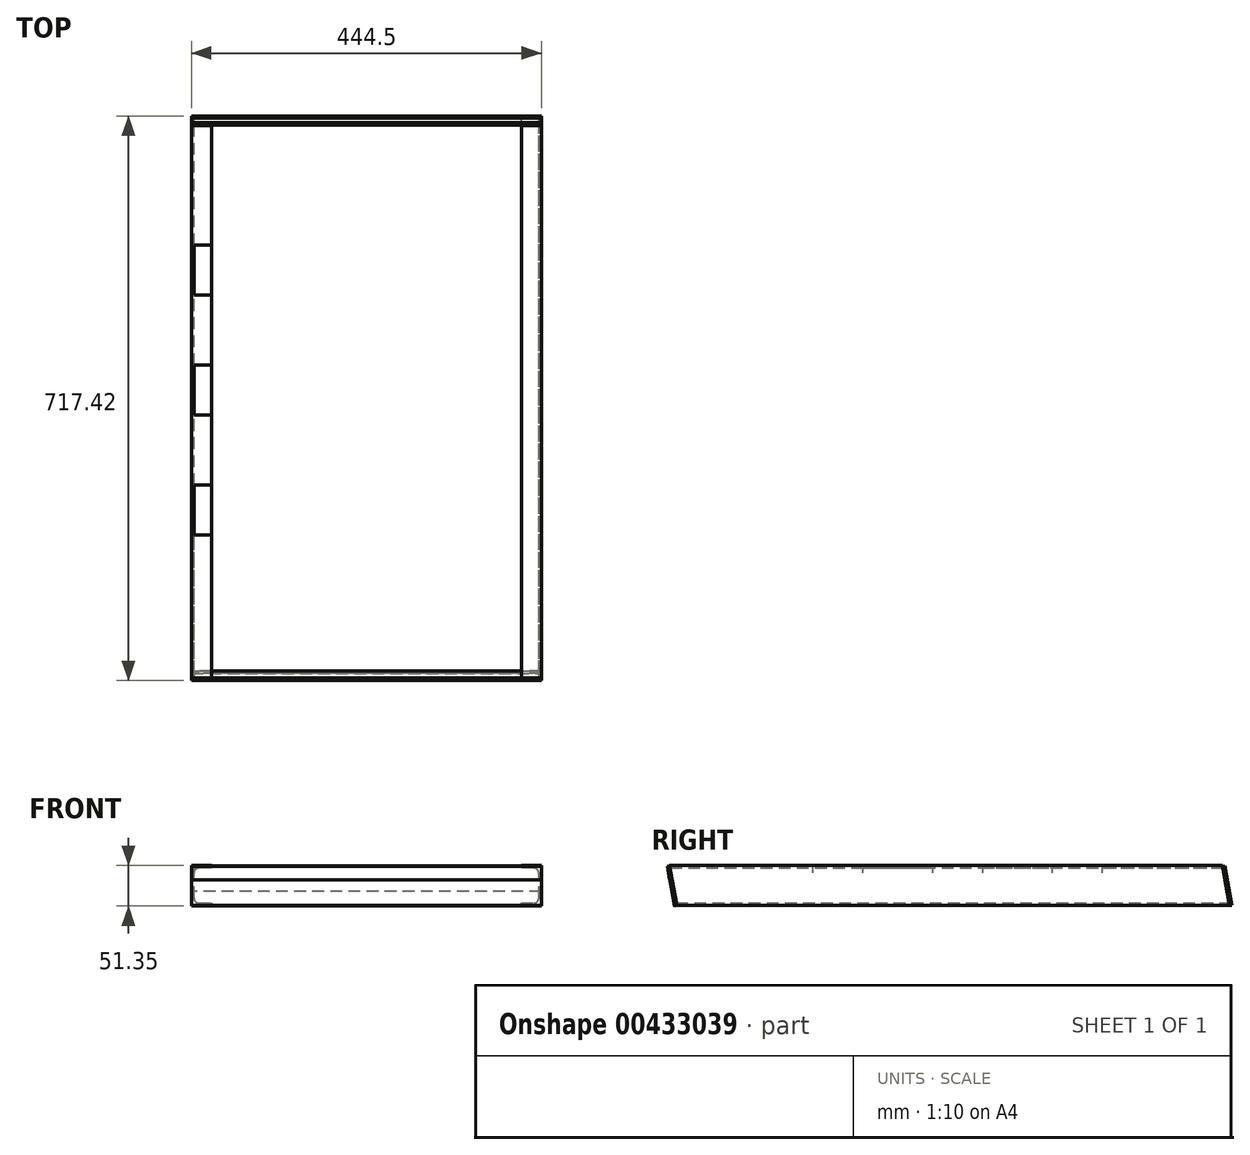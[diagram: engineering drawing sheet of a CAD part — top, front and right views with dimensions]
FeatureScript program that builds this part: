
annotation { "Feature Type Name" : "Feature", "Feature Type Description" : "" }
export const myFeature = defineFeature(function(context is Context, id is Id, definition is map)
    precondition{}
    {
        {
            var Q0;
            Q0=qCreatedBy(makeId("Front.planeOp"),FACE);
            var sketch = newSketch(context, id + "F0", { "sketchPlane" : qUnion([Q0])});
            skLineSegment(sketch, "E0", {"start": v(25.4, 50.8) * mm, "end": v(0, 50.8) * mm});
            skLineSegment(sketch, "E1", {"start": v(0, 50.8) * mm, "end": v(0, 0) * mm});
            skLineSegment(sketch, "E2", {"start": v(0, 0) * mm, "end": v(25.4, 0) * mm});
            skLineSegment(sketch, "E3", {"start": v(25.4, 0) * mm, "end": v(25.4, 3.18) * mm});
            skLineSegment(sketch, "E4", {"start": v(25.4, 3.18) * mm, "end": v(9.53, 3.17) * mm});
            skLineSegment(sketch, "E5", {"start": v(3.18, 9.52) * mm, "end": v(3.17, 41.28) * mm});
            skLineSegment(sketch, "E6", {"start": v(9.52, 47.63) * mm, "end": v(25.4, 47.63) * mm});
            skLineSegment(sketch, "E7", {"start": v(25.4, 47.63) * mm, "end": v(25.4, 50.8) * mm});
            skLineSegment(sketch, "E8", {"start": v(419.1, 50.8) * mm, "end": v(419.1, 47.63) * mm});
            skLineSegment(sketch, "E9", {"start": v(419.1, 47.63) * mm, "end": v(434.98, 47.63) * mm});
            skLineSegment(sketch, "E10", {"start": v(441.33, 41.28) * mm, "end": v(441.33, 9.53) * mm});
            skLineSegment(sketch, "E11", {"start": v(434.98, 3.18) * mm, "end": v(419.1, 3.18) * mm});
            skLineSegment(sketch, "E12", {"start": v(419.1, 3.18) * mm, "end": v(419.1, 0) * mm});
            skLineSegment(sketch, "E13", {"start": v(419.1, 0) * mm, "end": v(444.5, 0) * mm});
            skLineSegment(sketch, "E14", {"start": v(444.5, 0) * mm, "end": v(444.5, 50.8) * mm});
            skLineSegment(sketch, "E15", {"start": v(444.5, 50.8) * mm, "end": v(419.1, 50.8) * mm});
            skPoint(sketch, "E16.visualSharp", {"position": v(3.17, 47.62) * mm});
            skArc(sketch, "E16.filletArc", {"start": v(9.52, 47.63) * mm, "mid": v(5.03, 45.77) * mm, "end": v(3.17, 41.28) * mm});
            skPoint(sketch, "E17.visualSharp", {"position": v(3.18, 3.17) * mm});
            skArc(sketch, "E17.filletArc", {"start": v(3.18, 9.52) * mm, "mid": v(5.03, 5.03) * mm, "end": v(9.53, 3.17) * mm});
            skPoint(sketch, "E18.visualSharp", {"position": v(441.33, 3.18) * mm});
            skArc(sketch, "E18.filletArc", {"start": v(434.98, 3.18) * mm, "mid": v(439.47, 5.03) * mm, "end": v(441.33, 9.53) * mm});
            skPoint(sketch, "E19.visualSharp", {"position": v(441.33, 47.63) * mm});
            skArc(sketch, "E19.filletArc", {"start": v(441.33, 41.28) * mm, "mid": v(439.47, 45.77) * mm, "end": v(434.98, 47.63) * mm});
            skSolve(sketch);
        }
        {
            var Q0;
            Q0=makeQuery(id+"F0.imprint","IMPRINT",FACE,{"disambiguationData":[TD([[makeQuery(id+"F0.imprint","IMPRINT",EDGE,{"derivedFrom":sQuery(id+"F0.wireOp",EDGE,"E0")}),1.0]])]});
            var Q1;
            Q1=makeQuery(id+"F0.imprint","IMPRINT",FACE,{"disambiguationData":[TD([[makeQuery(id+"F0.imprint","IMPRINT",EDGE,{"derivedFrom":sQuery(id+"F0.wireOp",EDGE,"E8")}),1.0]])]});
            extrude(context, id + "F1", {"entities" : qUnion([Q0, Q1]), "depth" : 711.2 * mm, "offsetDistance" : 25.4 * mm});
        }
        {
            var Q0;
            Q0=qCreatedBy(makeId("Right.planeOp"),FACE);
            var sketch = newSketch(context, id + "F2", { "sketchPlane" : qUnion([Q0])});
            skLineSegment(sketch, "E20", {"start": v(0, 0) * mm, "end": v(0, 50.8) * mm});
            skLineSegment(sketch, "E21", {"start": v(0, 50.8) * mm, "end": v(-8.96, 50.8) * mm});
            skLineSegment(sketch, "E22", {"start": v(-8.96, 50.8) * mm, "end": v(0, 0) * mm});
            skLineSegment(sketch, "E23", {"start": v(-702.24, 0) * mm, "end": v(-711.2, 50.8) * mm});
            skLineSegment(sketch, "E24", {"start": v(-711.2, 50.8) * mm, "end": v(-711.2, 0) * mm});
            skLineSegment(sketch, "E25", {"start": v(-711.2, 0) * mm, "end": v(-702.24, 0) * mm});
            skSolve(sketch);
        }
        {
            var Q0;
            Q0=makeQuery(id+"F2.imprint","IMPRINT",FACE,{"disambiguationData":[TD([[makeQuery(id+"F2.imprint","IMPRINT",EDGE,{"derivedFrom":sQuery(id+"F2.wireOp",EDGE,"E20")}),1.0]])]});
            var Q1;
            Q1=makeQuery(id+"F2.imprint","IMPRINT",FACE,{"disambiguationData":[TD([[makeQuery(id+"F2.imprint","IMPRINT",EDGE,{"derivedFrom":sQuery(id+"F2.wireOp",EDGE,"E23")}),1.0]])]});
            extrude(context, id + "F3", {"entities" : qUnion([Q0, Q1]), "operationType" : NewBodyOperationType.REMOVE, "endBound" : BoundingType.THROUGH_ALL, "depth" : 25.4 * mm});
        }
        {
            var Q0;
            Q0=qCreatedBy(makeId("Right.planeOp"),FACE);
            var sketch = newSketch(context, id + "F4", { "sketchPlane" : qUnion([Q0])});
            skLineSegment(sketch, "E26", {"start": v(0, 0) * mm, "end": v(3.13, 0.55) * mm});
            skLineSegment(sketch, "E27", {"start": v(3.13, 0.55) * mm, "end": v(-5.7, 50.58) * mm});
            skLineSegment(sketch, "E28", {"start": v(-5.7, 50.58) * mm, "end": v(-8.82, 50.03) * mm});
            skLineSegment(sketch, "E29", {"start": v(-8.82, 50.03) * mm, "end": v(0, 0) * mm});
            skLineSegment(sketch, "E30", {"start": v(-702.24, 0) * mm, "end": v(-711.16, 50.58) * mm});
            skLineSegment(sketch, "E31", {"start": v(-711.16, 50.58) * mm, "end": v(-714.29, 50.03) * mm});
            skLineSegment(sketch, "E32", {"start": v(-714.29, 50.03) * mm, "end": v(-705.37, -0.55) * mm});
            skLineSegment(sketch, "E33", {"start": v(-705.37, -0.55) * mm, "end": v(-702.24, 0) * mm});
            skSolve(sketch);
        }
        {
            var Q0;
            Q0=makeQuery(id+"F4.imprint","IMPRINT",FACE,{"disambiguationData":[TD([[makeQuery(id+"F4.imprint","IMPRINT",EDGE,{"derivedFrom":sQuery(id+"F4.wireOp",EDGE,"E26")}),1.0]])]});
            var Q1;
            Q1=makeQuery(id+"F4.imprint","IMPRINT",FACE,{"disambiguationData":[TD([[makeQuery(id+"F4.imprint","IMPRINT",EDGE,{"derivedFrom":sQuery(id+"F4.wireOp",EDGE,"E30")}),1.0]])]});
            extrude(context, id + "F5", {"entities" : qUnion([Q0, Q1]), "depth" : 444.5 * mm, "offsetDistance" : 25.4 * mm});
        }
        {
            var Q0;
            Q0=makeQuery(id+"F1.opExtrude","SWEPT_FACE",FACE,{"disambiguationData":[OSD([sQuery(id+"F0.wireOp",EDGE,"E0")])]});
            var sketch = newSketch(context, id + "F6", { "sketchPlane" : qUnion([Q0])});
            skLineSegment(sketch, "E34.bottom", {"start": v(25.4, -161.22) * mm, "end": v(3.17, -161.22) * mm});
            skLineSegment(sketch, "E34.top", {"start": v(25.4, -224.72) * mm, "end": v(3.18, -224.72) * mm});
            skLineSegment(sketch, "E34.left", {"start": v(25.4, -161.22) * mm, "end": v(25.4, -224.72) * mm});
            skLineSegment(sketch, "E34.right", {"start": v(3.18, -161.22) * mm, "end": v(3.18, -224.72) * mm});
            skLineSegment(sketch, "E35.bottom", {"start": v(25.4, -313.62) * mm, "end": v(3.17, -313.62) * mm});
            skLineSegment(sketch, "E35.top", {"start": v(25.4, -377.12) * mm, "end": v(3.18, -377.12) * mm});
            skLineSegment(sketch, "E35.left", {"start": v(25.4, -313.62) * mm, "end": v(25.4, -377.12) * mm});
            skLineSegment(sketch, "E35.right", {"start": v(3.17, -313.62) * mm, "end": v(3.18, -377.12) * mm});
            skLineSegment(sketch, "E36.bottom", {"start": v(25.4, -466.02) * mm, "end": v(3.17, -466.02) * mm});
            skLineSegment(sketch, "E36.top", {"start": v(25.4, -529.52) * mm, "end": v(3.18, -529.52) * mm});
            skLineSegment(sketch, "E36.left", {"start": v(25.4, -466.02) * mm, "end": v(25.4, -529.52) * mm});
            skLineSegment(sketch, "E36.right", {"start": v(3.17, -466.02) * mm, "end": v(3.18, -529.52) * mm});
            skSolve(sketch);
        }
        {
            var Q0;
            Q0=makeQuery(id+"F6.imprint","IMPRINT",FACE,{"disambiguationData":[TD([[makeQuery(id+"F6.imprint","IMPRINT",EDGE,{"derivedFrom":sQuery(id+"F6.wireOp",EDGE,"E34.bottom")}),1.0]])]});
            var Q1;
            Q1=makeQuery(id+"F6.imprint","IMPRINT",FACE,{"disambiguationData":[TD([[makeQuery(id+"F6.imprint","IMPRINT",EDGE,{"derivedFrom":sQuery(id+"F6.wireOp",EDGE,"E35.bottom")}),1.0]])]});
            var Q2;
            Q2=makeQuery(id+"F6.imprint","IMPRINT",FACE,{"disambiguationData":[TD([[makeQuery(id+"F6.imprint","IMPRINT",EDGE,{"derivedFrom":sQuery(id+"F6.wireOp",EDGE,"E36.bottom")}),1.0]])]});
            extrude(context, id + "F7", {"entities" : qUnion([Q0, Q1, Q2]), "operationType" : NewBodyOperationType.REMOVE, "oppositeDirection" : true, "depth" : 25.4 * mm});
        }
    });
